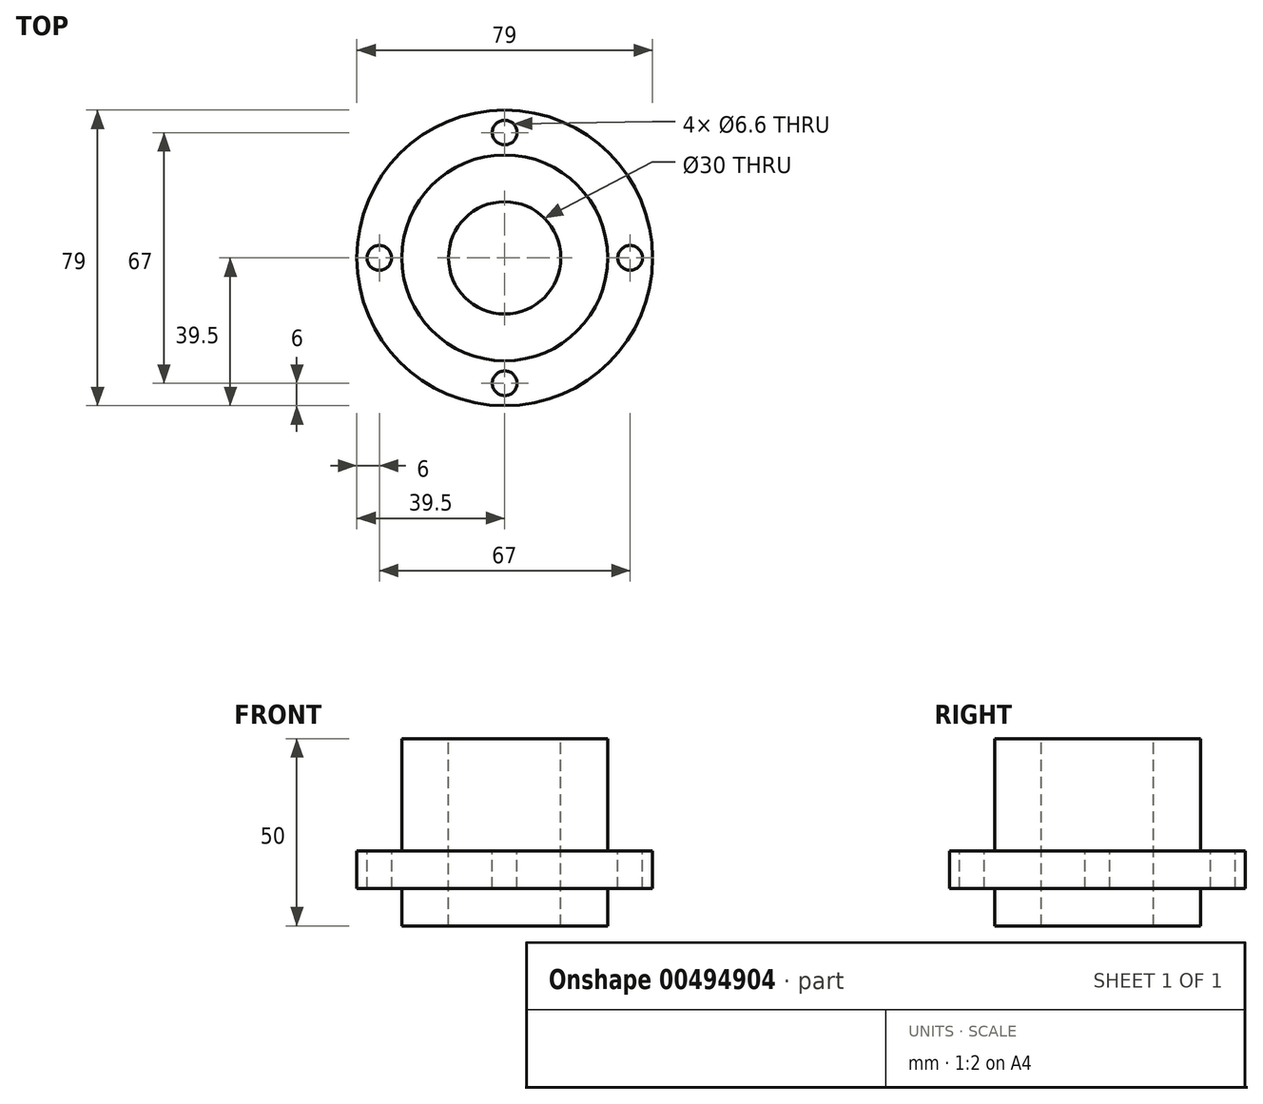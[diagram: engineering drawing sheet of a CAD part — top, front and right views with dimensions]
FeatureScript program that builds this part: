
annotation { "Feature Type Name" : "Feature", "Feature Type Description" : "" }
export const myFeature = defineFeature(function(context is Context, id is Id, definition is map)
    precondition{}
    {
        {
            var Q0;
            Q0=qCreatedBy(makeId("Top.planeOp"),FACE);
            var sketch = newSketch(context, id + "F0", { "sketchPlane" : qUnion([Q0])});
            skCircle(sketch, "E0", {"center": v(0, 0) * mm, "radius": 27.5 * mm});
            skSolve(sketch);
        }
        {
            var Q0;
            Q0=qSketchRegion(id+"F0",true);
            extrude(context, id + "F1", {"entities" : qUnion([Q0]), "oppositeDirection" : true, "depth" : 10 * mm});
        }
        {
            var Q0;
            Q0=qCreatedBy(makeId("Top.planeOp"),FACE);
            var sketch = newSketch(context, id + "F2", { "sketchPlane" : qUnion([Q0])});
            skCircle(sketch, "E1", {"center": v(0, 0) * mm, "radius": 39.5 * mm});
            skSolve(sketch);
        }
        {
            var Q0;
            Q0=qSketchRegion(id+"F2",true);
            extrude(context, id + "F3", {"entities" : qUnion([Q0]), "operationType" : NewBodyOperationType.ADD, "depth" : 10 * mm});
        }
        {
            var Q0;
            Q0=makeQuery(id+"F3.opExtrude","CAP_FACE",FACE,{"disambiguationData":[OSD([sQuery(id+"F2.wireOp",EDGE,"E1")])],"isStart":false});
            var sketch = newSketch(context, id + "F4", { "sketchPlane" : qUnion([Q0])});
            skCircle(sketch, "E2", {"center": v(0, 0) * mm, "radius": 27.5 * mm});
            skSolve(sketch);
        }
        {
            var Q0;
            Q0=qSketchRegion(id+"F4",true);
            extrude(context, id + "F5", {"entities" : qUnion([Q0]), "operationType" : NewBodyOperationType.ADD, "depth" : 30 * mm});
        }
        {
            var Q0;
            Q0=makeQuery(id+"F5.opExtrude","CAP_FACE",FACE,{"disambiguationData":[OSD([sQuery(id+"F4.wireOp",EDGE,"E2")])],"isStart":false});
            var sketch = newSketch(context, id + "F6", { "sketchPlane" : qUnion([Q0])});
            skCircle(sketch, "E3", {"center": v(0, 0) * mm, "radius": 15 * mm});
            skSolve(sketch);
        }
        {
            var Q0;
            Q0=qSketchRegion(id+"F6",true);
            extrude(context, id + "F7", {"entities" : qUnion([Q0]), "operationType" : NewBodyOperationType.REMOVE, "endBound" : BoundingType.THROUGH_ALL, "oppositeDirection" : true, "depth" : 25 * mm});
        }
        {
            var Q0;
            Q0=makeQuery(id+"F3.opExtrude","CAP_FACE",FACE,{"disambiguationData":[OSD([sQuery(id+"F2.wireOp",EDGE,"E1")])],"isStart":false});
            var sketch = newSketch(context, id + "F8", { "sketchPlane" : qUnion([Q0])});
            skPoint(sketch, "E4", {"position": v(0, 33.5) * mm});
            skPoint(sketch, "E5", {"position": v(33.5, 0) * mm});
            skPoint(sketch, "E6", {"position": v(0, -33.5) * mm});
            skPoint(sketch, "E7", {"position": v(-33.5, 0) * mm});
            skSolve(sketch);
        }
        {
            var Q0;
            Q0=sQuery(id+"F8.wireOp",VERTEX,"E4");
            var Q1;
            Q1=sQuery(id+"F8.wireOp",VERTEX,"E5");
            var Q2;
            Q2=sQuery(id+"F8.wireOp",VERTEX,"E6");
            var Q3;
            Q3=sQuery(id+"F8.wireOp",VERTEX,"E7");
            var Q4;
            Q4=makeQuery(id+"F1.opExtrude","SWEPT_BODY",BODY,{"disambiguationData":[OSD([sQuery(id+"F0.wireOp",EDGE,"E0")])]});
            hole(context, id + "F9", {"style" : HoleStyle.SIMPLE, "endStyle" : HoleEndStyle.THROUGH, "holeDiameter" : 6.6 * mm, "isTappedThrough" : true, "tappedDepth" : 12.25 * mm, "tapClearance" : 3, "locations" : qUnion([Q0, Q1, Q2, Q3]), "scope" : qUnion([Q4])});
        }
    });
